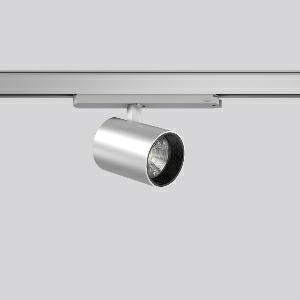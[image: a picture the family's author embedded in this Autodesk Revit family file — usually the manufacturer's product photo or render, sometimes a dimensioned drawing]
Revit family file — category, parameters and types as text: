
# Revit family: deecos_s_mini_track-in_742256_004_1_730_255b
name_source: partatom
category: Lighting Fixtures
units: mm (PartAtom-declared; Revit-internal decimal feet)

## family parameters
Cut with Voids When Loaded = No
Host = Face
Light Source = No
Part Type = Normal
Room Calculation Point = No
Round Connector Dimension = Use Diameter
Shared = No

## types (1)
- DEECOS S mini track-in (1 x LED Modul 940, 2450 lm, 4000)
    Apparent Load = 20 VA
    Approval mark = CE
    CIE Flux Codes = 80 99 100 100 100
    Color Rendering = 92
    Color Temperature = 4000
    Default Elevation = 1800 mm
    Description = Series: DEECOS S mini track-in
LED surface-mounted projector in modern design with no visible cooling ribs. Housing: die-cast aluminium, powder-coated. Rotation range: 356°. Swivel range: 90°. Black plastic ring and recessed LED to prevent glare from the side. Optical assembly with lens made of plastic (polycarbonate) for the best homogeneous light distribution - can be changed without tools. Best colour rendering index Ra>90. With multi adaptor for 3-circuit tracks 230 V. Suitable for Track on ceiling, Wall track. Track-in driver integrated into the adapter. High quality converter without flickering and stroboscopic effect. With Casambi smart+free Bluetooth control for wireless network and operation using Android / iOS devices, free app available for download. The following accessories can be mounted without use of tools: interchangeable lenses, decorative glasses, honeycomb louvre, clear and frosted diffusers, white interchangeable plastic ring. 
Colour: silver
Diameter: 87 mm
Height: 135 mm
Lamp: LED
Socket: without socket
Colour temperature: 4000K
Colour rendering index (CRI): 92
System power: 20 W
Rated luminous flux: 2450 lm
Luminous efficiency: 123 lm/W
Control gear: Dimmable Bluetooth converter
Protection class: II
Type of protection: IP 20
    Height = 135 mm
    Lamp = 1 x LED Modul 940
    Lamp Light Flux = 2450 lm
    Lamp count = 1
    Length = 87 mm
    Lifetime = 50000 h
    Luminous efficacy = 123 lm/W
    Manufacturer = RZB
    ModVariant = No
    Model = 742256.004.1.730
    Mounting Place = Ceiling
    Mounting Type = Rail mounted
    Number of Poles = 1
    OnlyDefault = Yes
    Power Factor = 1
    Product Name = DEECOS S mini track-in
    Product group = Track mounted projectors
    ProductGroupID = 301
    Protection Class = Protection class II
    Protection Degree = IP 20
    RLX_Detail_Level = 1
    RLX_Emergency_Light_Flux = 0 lm
    RLX_Emergency_Type = 0
    RLX_Emergency_Type_DB = No
    RlxData = <blob elided: 36621 chars, md5=b9482c0b>
    Socket = socket
    Standby Power = 0 W
    System Light Flux = 2450 lm
    System Power = 20 W
    Type Comments = Product without accessories
    Type Image = 742108.004.jpg
    URL = http://relux.com
    VarID = ---
    Voltage = 230 V
    Voltage Range = 220-240 V
    Weight = 0.00 kg
    Width = 0 mm  [stored 0 ft]

note: [stored X ft] marks values corroborated as IEEE doubles in the binary element streams (Revit-internal decimal feet)

## geometry (parser evidence)
native form markers: Blend x4, Sweep x15
no freeform markers — native parametric forms only
